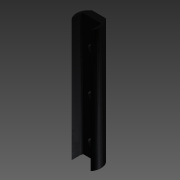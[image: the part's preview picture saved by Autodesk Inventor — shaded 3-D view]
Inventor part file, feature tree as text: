
AUTODESK INVENTOR PART (.ipt)
format: ipt  version: 2015 (Build 190159000, 159)  size: 114,688 bytes
history: native  units: mm
features: sketch x3, extrude x2, other x1, hole x1
ambient origin geometry x8: Origin, YZ Plane, XZ Plane, XY Plane, X Axis, Y Axis, Z Axis, Center Point
bodies: Body1 (feature_tree)
feature tree (7):
  other  "Bryła1"
  extrude  "Wyciągnięcie proste1"  Depth=18.0mm
  extrude  "Wyciągnięcie proste2"  Depth=90.0mm TaperAngle=0.0deg
  hole  "Otwór1"  [1 undecoded]
  sketch  "Szkic1"
  sketch  "Szkic2"
  sketch  "Szkic3"
note: 1 required parameter value undecoded (feature->parameter linkage not recoverable at this tier; creation-order binding heuristic only, values carry confidence <= 0.55)
